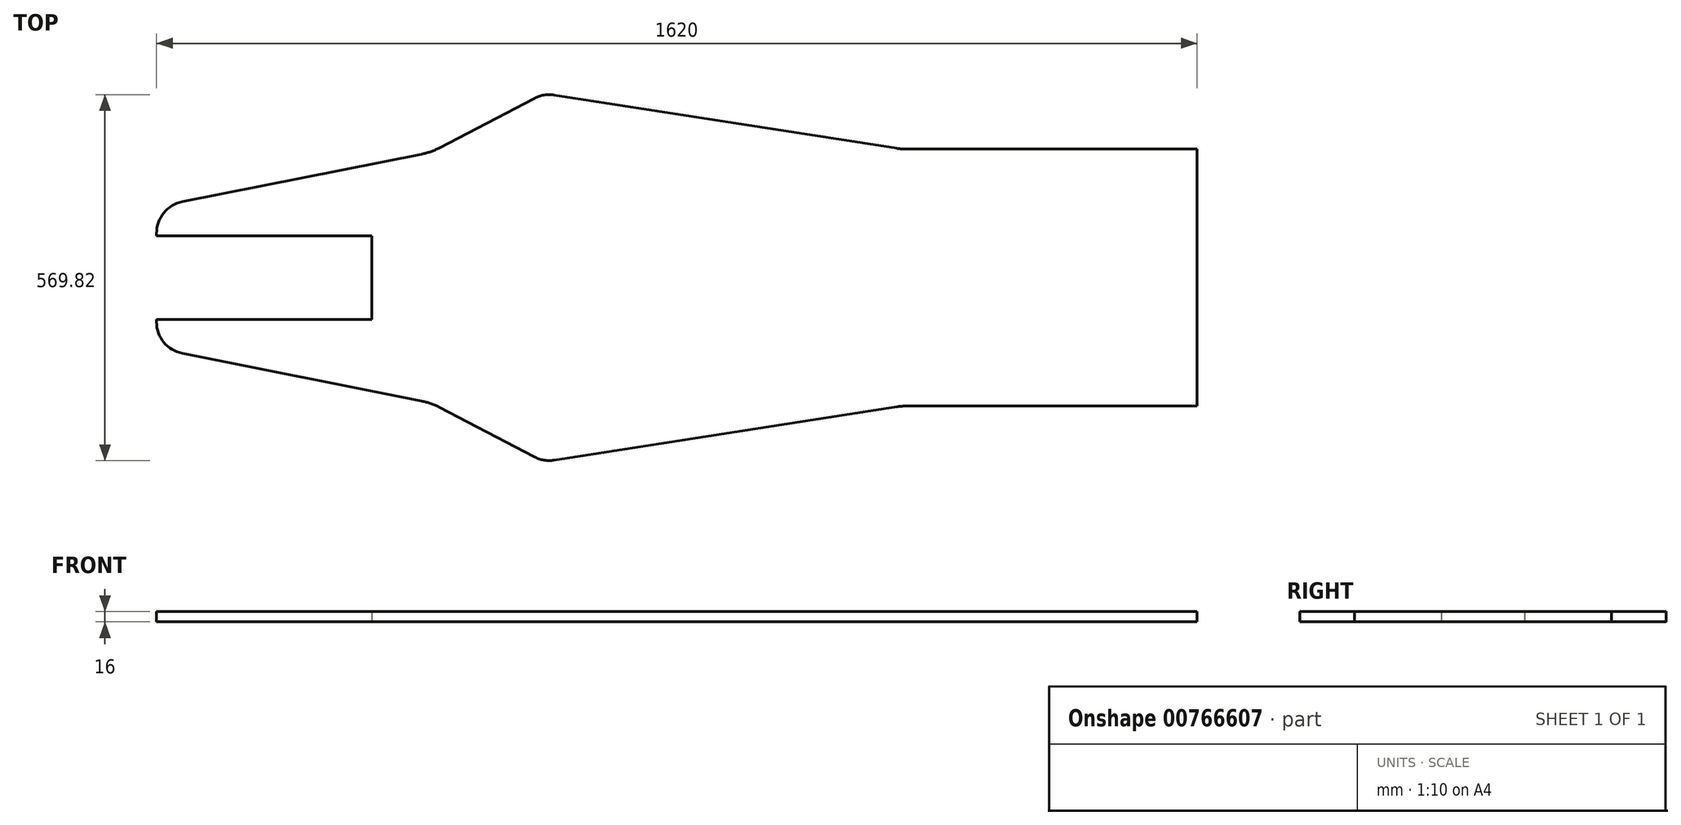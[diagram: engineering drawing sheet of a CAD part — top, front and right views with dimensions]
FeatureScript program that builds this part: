
annotation { "Feature Type Name" : "Feature", "Feature Type Description" : "" }
export const myFeature = defineFeature(function(context is Context, id is Id, definition is map)
    precondition{}
    {
        {
            var Q0;
            Q0=qCreatedBy(makeId("Top.planeOp"),FACE);
            var sketch = newSketch(context, id + "F0", { "sketchPlane" : qUnion([Q0])});
            skLineSegment(sketch, "E0", {"start": v(-860, 0) * mm, "end": v(860, 0) * mm, "construction": true});
            skLineSegment(sketch, "E1", {"start": v(-475, -65) * mm, "end": v(-475, 65) * mm});
            skLineSegment(sketch, "E2", {"start": v(810, 200) * mm, "end": v(810, -200) * mm});
            skLineSegment(sketch, "E3", {"start": v(357.75, -200) * mm, "end": v(810, -200) * mm});
            skLineSegment(sketch, "E4", {"start": v(357.75, 200) * mm, "end": v(810, 200) * mm});
            skLineSegment(sketch, "E5", {"start": v(-810, 68.97) * mm, "end": v(-810, 65) * mm});
            skLineSegment(sketch, "E6", {"start": v(342.34, -201.2) * mm, "end": v(-190.75, -284.32) * mm});
            skLineSegment(sketch, "E7", {"start": v(-221.58, -279.24) * mm, "end": v(-370.3, -201.63) * mm});
            skLineSegment(sketch, "E8", {"start": v(-769.76, -118) * mm, "end": v(-397.05, -192.2) * mm});
            skLineSegment(sketch, "E9", {"start": v(-810, -65) * mm, "end": v(-475, -65) * mm});
            skLineSegment(sketch, "E10", {"start": v(-810, 65) * mm, "end": v(-475, 65) * mm});
            skLineSegment(sketch, "E11", {"start": v(342.34, 201.2) * mm, "end": v(-190.75, 284.32) * mm});
            skLineSegment(sketch, "E12", {"start": v(-221.58, 279.24) * mm, "end": v(-370.3, 201.63) * mm});
            skLineSegment(sketch, "E13", {"start": v(-769.76, 118) * mm, "end": v(-397.05, 192.2) * mm});
            skLineSegment(sketch, "E14", {"start": v(-810, -65) * mm, "end": v(-810, -68.97) * mm});
            skArc(sketch, "E15", {"start": v(-190.75, 284.32) * mm, "mid": v(-206.57, 284.25) * mm, "end": v(-221.58, 279.24) * mm});
            skArc(sketch, "E16", {"start": v(-221.58, -279.24) * mm, "mid": v(-206.57, -284.25) * mm, "end": v(-190.75, -284.32) * mm});
            skArc(sketch, "E17", {"start": v(-810, -68.97) * mm, "mid": v(-798.65, -100.69) * mm, "end": v(-769.76, -118) * mm});
            skArc(sketch, "E18", {"start": v(-769.76, 118) * mm, "mid": v(-798.65, 100.69) * mm, "end": v(-810, 68.97) * mm});
            skArc(sketch, "E19", {"start": v(-370.3, -201.63) * mm, "mid": v(-383.34, -195.96) * mm, "end": v(-397.05, -192.2) * mm});
            skArc(sketch, "E20", {"start": v(-397.05, 192.2) * mm, "mid": v(-383.34, 195.96) * mm, "end": v(-370.3, 201.63) * mm});
            skArc(sketch, "E21", {"start": v(357.75, -200) * mm, "mid": v(350.02, -200.3) * mm, "end": v(342.34, -201.2) * mm});
            skArc(sketch, "E22", {"start": v(342.34, 201.2) * mm, "mid": v(350.02, 200.3) * mm, "end": v(357.75, 200) * mm});
            skSolve(sketch);
        }
        {
            var Q0;
            Q0 = qSketchRegion(id + "F0", true);
            extrude(context, id + "F1", {"entities" : qUnion([Q0]), "endBound" : BoundingType.SYMMETRIC, "depth" : 16 * mm, "offsetDistance" : 25 * mm});
        }
    });
